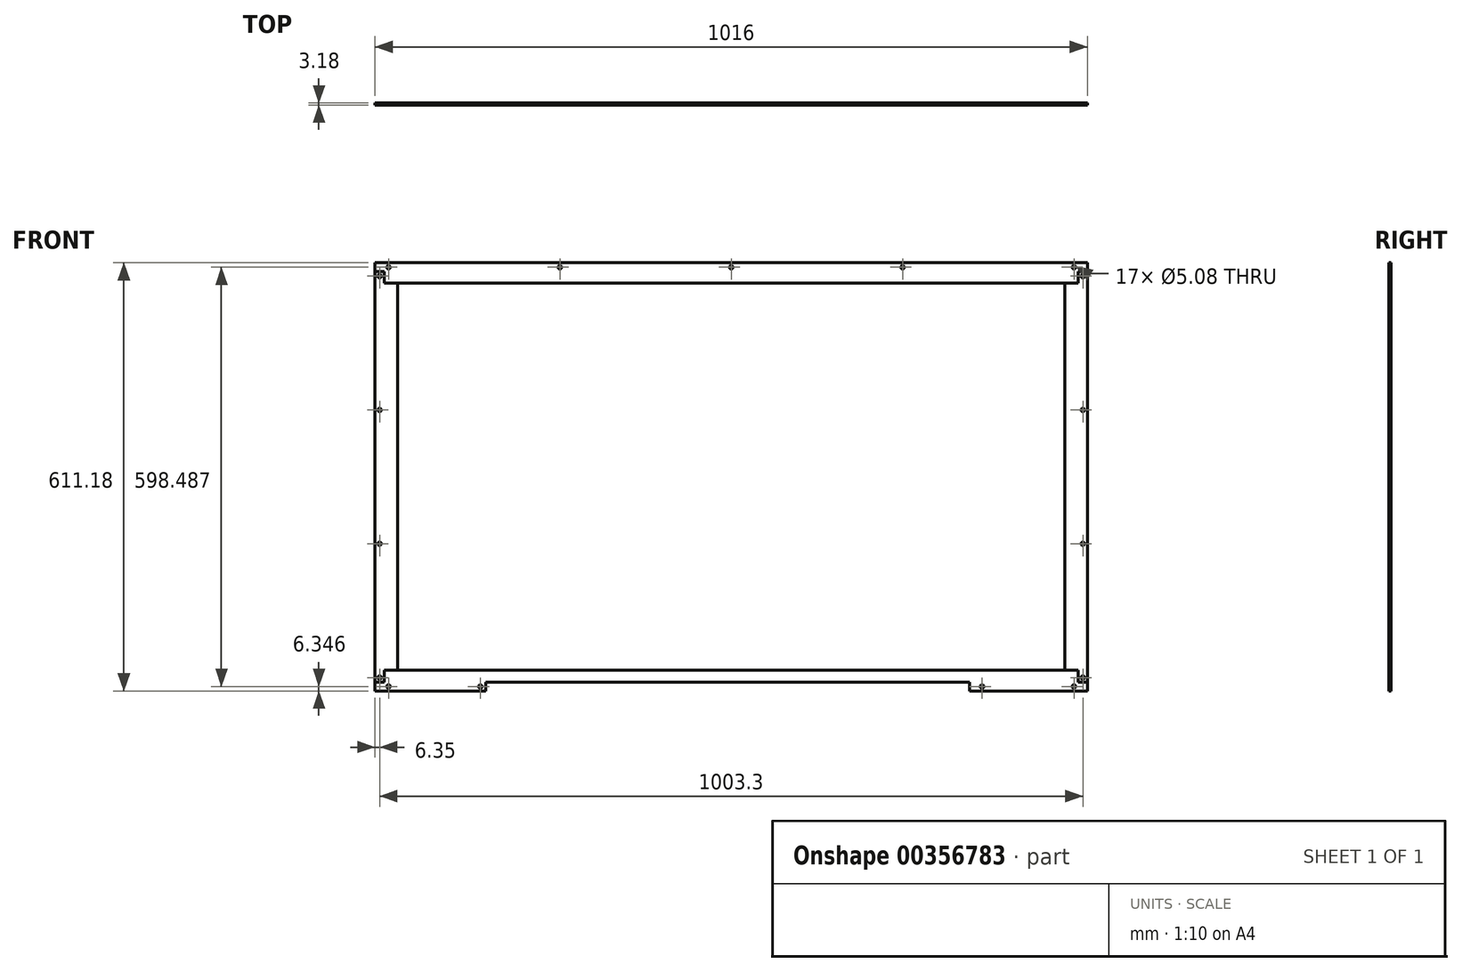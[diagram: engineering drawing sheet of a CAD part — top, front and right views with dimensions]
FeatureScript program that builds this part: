
annotation { "Feature Type Name" : "Feature", "Feature Type Description" : "" }
export const myFeature = defineFeature(function(context is Context, id is Id, definition is map)
    precondition{}
    {
        {
            var Q0;
            Q0=qCreatedBy(makeId("Front.planeOp"),FACE);
            var sketch = newSketch(context, id + "F0", { "sketchPlane" : qUnion([Q0])});
            skLineSegment(sketch, "E0.bottom", {"start": v(495.3, 292.9) * mm, "end": v(-495.3, 292.9) * mm});
            skLineSegment(sketch, "E0.top", {"start": v(495.3, -292.9) * mm, "end": v(-495.3, -292.9) * mm});
            skLineSegment(sketch, "E0.left", {"start": v(495.3, 292.9) * mm, "end": v(495.3, -292.9) * mm});
            skLineSegment(sketch, "E0.right", {"start": v(-495.3, 292.9) * mm, "end": v(-495.3, -292.9) * mm});
            skPoint(sketch, "E0.middle", {"position": v(0, 0) * mm});
            skLineSegment(sketch, "E1.0", {"start": v(-508, 305.6) * mm, "end": v(-508, -305.6) * mm});
            skLineSegment(sketch, "E1.1", {"start": v(508, 305.6) * mm, "end": v(-508, 305.6) * mm});
            skLineSegment(sketch, "E1.2", {"start": v(508, 305.6) * mm, "end": v(508, -305.6) * mm});
            skLineSegment(sketch, "E1.3", {"start": v(508, -305.6) * mm, "end": v(-508, -305.6) * mm});
            skLineSegment(sketch, "E2", {"start": v(-508, 305.6) * mm, "end": v(-495.3, 292.9) * mm});
            skPoint(sketch, "E3.middle", {"position": v(-501.65, 299.24) * mm});
            skLineSegment(sketch, "E4.bottom", {"start": v(-355.3, -296.7) * mm, "end": v(-360.38, -296.7) * mm});
            skLineSegment(sketch, "E4.top", {"start": v(-355.3, -301.78) * mm, "end": v(-360.38, -301.78) * mm});
            skLineSegment(sketch, "E4.left", {"start": v(-355.3, -296.7) * mm, "end": v(-355.3, -301.78) * mm});
            skLineSegment(sketch, "E4.right", {"start": v(-360.38, -296.7) * mm, "end": v(-360.38, -301.78) * mm});
            skPoint(sketch, "E4.middle", {"position": v(-357.84, -299.24) * mm});
            skLineSegment(sketch, "E5.MirrorCS", {"start": v(360.38, -296.7) * mm, "end": v(360.38, -301.78) * mm});
            skLineSegment(sketch, "E6.MirrorCS", {"start": v(355.3, -296.7) * mm, "end": v(360.38, -296.7) * mm});
            skLineSegment(sketch, "E7.MirrorCS", {"start": v(355.3, -296.7) * mm, "end": v(355.3, -301.78) * mm});
            skLineSegment(sketch, "E8.MirrorCS", {"start": v(355.3, -301.78) * mm, "end": v(360.38, -301.78) * mm});
            skLineSegment(sketch, "E9.bottom", {"start": v(-486.41, 296.7) * mm, "end": v(-491.5, 296.7) * mm});
            skLineSegment(sketch, "E9.top", {"start": v(-486.41, 301.78) * mm, "end": v(-491.5, 301.78) * mm});
            skLineSegment(sketch, "E9.left", {"start": v(-486.41, 296.7) * mm, "end": v(-486.41, 301.78) * mm});
            skLineSegment(sketch, "E9.right", {"start": v(-491.5, 296.7) * mm, "end": v(-491.5, 301.78) * mm});
            skPoint(sketch, "E9.middle", {"position": v(-488.95, 299.24) * mm});
            skLineSegment(sketch, "E10.MirrorCS", {"start": v(-504.2, 284) * mm, "end": v(-504.2, 289.08) * mm});
            skLineSegment(sketch, "E11.MirrorCS", {"start": v(-499.11, 289.08) * mm, "end": v(-504.2, 289.08) * mm});
            skLineSegment(sketch, "E12.MirrorCS", {"start": v(-499.11, 284) * mm, "end": v(-499.11, 289.08) * mm});
            skLineSegment(sketch, "E13.MirrorCS", {"start": v(-499.11, 284) * mm, "end": v(-504.2, 284) * mm});
            skCircle(sketch, "E14", {"center": v(-488.95, 299.24) * mm, "radius": 5.97 * mm});
            skLineSegment(sketch, "E15.MirrorCS", {"start": v(499.11, 284) * mm, "end": v(499.11, 289.08) * mm});
            skLineSegment(sketch, "E16.MirrorCS", {"start": v(499.11, 284) * mm, "end": v(504.2, 284) * mm});
            skLineSegment(sketch, "E17.MirrorCS", {"start": v(499.11, 289.08) * mm, "end": v(504.2, 289.08) * mm});
            skLineSegment(sketch, "E18.MirrorCS", {"start": v(504.2, 284) * mm, "end": v(504.2, 289.08) * mm});
            skLineSegment(sketch, "E19.MirrorCS", {"start": v(486.41, 301.78) * mm, "end": v(491.5, 301.78) * mm});
            skLineSegment(sketch, "E20.MirrorCS", {"start": v(486.41, 296.7) * mm, "end": v(486.41, 301.78) * mm});
            skLineSegment(sketch, "E21.MirrorCS", {"start": v(486.41, 296.7) * mm, "end": v(491.5, 296.7) * mm});
            skLineSegment(sketch, "E22.MirrorCS", {"start": v(491.5, 296.7) * mm, "end": v(491.5, 301.78) * mm});
            skPoint(sketch, "E23.MirrorP", {"position": v(488.95, 299.24) * mm});
            skLineSegment(sketch, "E24.MirrorCS", {"start": v(-499.11, -289.08) * mm, "end": v(-504.2, -289.08) * mm});
            skLineSegment(sketch, "E25.MirrorCS", {"start": v(-499.1, -284) * mm, "end": v(-499.1, -289.08) * mm});
            skLineSegment(sketch, "E26.MirrorCS", {"start": v(-499.11, -284) * mm, "end": v(-504.2, -284) * mm});
            skLineSegment(sketch, "E27.MirrorCS", {"start": v(-504.2, -284) * mm, "end": v(-504.2, -289.08) * mm});
            skLineSegment(sketch, "E28.MirrorCS", {"start": v(-486.41, -301.78) * mm, "end": v(-491.5, -301.78) * mm});
            skLineSegment(sketch, "E29.MirrorCS", {"start": v(-491.5, -296.7) * mm, "end": v(-491.5, -301.78) * mm});
            skPoint(sketch, "E30.MirrorP", {"position": v(-488.95, -299.24) * mm});
            skLineSegment(sketch, "E31.MirrorCS", {"start": v(-486.41, -296.7) * mm, "end": v(-486.41, -301.78) * mm});
            skLineSegment(sketch, "E32.MirrorCS", {"start": v(-486.41, -296.7) * mm, "end": v(-491.5, -296.7) * mm});
            skLineSegment(sketch, "E33.MirrorCS", {"start": v(486.41, -296.7) * mm, "end": v(486.41, -301.78) * mm});
            skPoint(sketch, "E34.MirrorP", {"position": v(488.95, -299.24) * mm});
            skLineSegment(sketch, "E35.MirrorCS", {"start": v(491.5, -296.7) * mm, "end": v(491.5, -301.78) * mm});
            skLineSegment(sketch, "E36.MirrorCS", {"start": v(486.41, -296.7) * mm, "end": v(491.5, -296.7) * mm});
            skLineSegment(sketch, "E37.MirrorCS", {"start": v(486.41, -301.78) * mm, "end": v(491.5, -301.78) * mm});
            skLineSegment(sketch, "E38.MirrorCS", {"start": v(499.11, -289.08) * mm, "end": v(504.2, -289.08) * mm});
            skLineSegment(sketch, "E39.MirrorCS", {"start": v(504.2, -284) * mm, "end": v(504.2, -289.08) * mm});
            skLineSegment(sketch, "E40.MirrorCS", {"start": v(499.11, -284) * mm, "end": v(499.11, -289.08) * mm});
            skLineSegment(sketch, "E41.MirrorCS", {"start": v(499.11, -284) * mm, "end": v(504.2, -284) * mm});
            skLineSegment(sketch, "E42.bottom", {"start": v(-504.19, 92.97) * mm, "end": v(-499.11, 92.97) * mm});
            skLineSegment(sketch, "E42.top", {"start": v(-504.19, 98.05) * mm, "end": v(-499.11, 98.05) * mm});
            skLineSegment(sketch, "E42.left", {"start": v(-504.2, 92.97) * mm, "end": v(-504.2, 98.05) * mm});
            skLineSegment(sketch, "E42.right", {"start": v(-499.11, 92.97) * mm, "end": v(-499.11, 98.05) * mm});
            skPoint(sketch, "E42.middle", {"position": v(-501.65, 95.51) * mm});
            skLineSegment(sketch, "E43.bottom", {"start": v(-499.11, -92.97) * mm, "end": v(-504.19, -92.97) * mm});
            skLineSegment(sketch, "E43.top", {"start": v(-499.11, -98.05) * mm, "end": v(-504.19, -98.05) * mm});
            skLineSegment(sketch, "E43.left", {"start": v(-499.11, -92.97) * mm, "end": v(-499.11, -98.05) * mm});
            skLineSegment(sketch, "E43.right", {"start": v(-504.2, -92.97) * mm, "end": v(-504.2, -98.05) * mm});
            skPoint(sketch, "E43.middle", {"position": v(-501.65, -95.51) * mm});
            skLineSegment(sketch, "E44", {"start": v(-501.65, -284) * mm, "end": v(-501.65, -98.05) * mm});
            skLineSegment(sketch, "E45", {"start": v(-501.65, -92.97) * mm, "end": v(-501.65, 92.97) * mm});
            skLineSegment(sketch, "E46", {"start": v(-501.65, 98.05) * mm, "end": v(-501.65, 284) * mm});
            skLineSegment(sketch, "E47.bottom", {"start": v(2.54, 301.78) * mm, "end": v(-2.54, 301.78) * mm});
            skLineSegment(sketch, "E47.top", {"start": v(2.54, 296.7) * mm, "end": v(-2.54, 296.7) * mm});
            skLineSegment(sketch, "E47.left", {"start": v(2.54, 301.78) * mm, "end": v(2.54, 296.7) * mm});
            skLineSegment(sketch, "E47.right", {"start": v(-2.54, 301.78) * mm, "end": v(-2.54, 296.7) * mm});
            skPoint(sketch, "E47.middle", {"position": v(0, 299.24) * mm});
            skPoint(sketch, "E47.middle.positionSnap0", {"position": v(0, 305.6) * mm});
            skPoint(sketch, "E47.centerSnap0", {"position": v(0, 305.6) * mm});
            skLineSegment(sketch, "E48.bottom", {"start": v(-241.94, 301.78) * mm, "end": v(-247.02, 301.78) * mm});
            skLineSegment(sketch, "E48.top", {"start": v(-241.94, 296.7) * mm, "end": v(-247.02, 296.7) * mm});
            skLineSegment(sketch, "E48.left", {"start": v(-241.94, 301.78) * mm, "end": v(-241.94, 296.7) * mm});
            skLineSegment(sketch, "E48.right", {"start": v(-247.02, 301.78) * mm, "end": v(-247.02, 296.7) * mm});
            skPoint(sketch, "E48.middle", {"position": v(-244.48, 299.24) * mm});
            skLineSegment(sketch, "E49.MirrorCS", {"start": v(241.94, 296.7) * mm, "end": v(247.02, 296.7) * mm});
            skPoint(sketch, "E50.MirrorP", {"position": v(244.48, 299.24) * mm});
            skLineSegment(sketch, "E51.MirrorCS", {"start": v(247.02, 301.78) * mm, "end": v(247.02, 296.7) * mm});
            skLineSegment(sketch, "E52.MirrorCS", {"start": v(241.94, 301.78) * mm, "end": v(247.02, 301.78) * mm});
            skLineSegment(sketch, "E53.MirrorCS", {"start": v(241.94, 301.78) * mm, "end": v(241.94, 296.7) * mm});
            skLineSegment(sketch, "E54.MirrorCS", {"start": v(504.19, 92.97) * mm, "end": v(499.11, 92.97) * mm});
            skLineSegment(sketch, "E55.MirrorCS", {"start": v(499.11, 92.97) * mm, "end": v(499.11, 98.05) * mm});
            skPoint(sketch, "E56.MirrorP", {"position": v(501.65, 95.51) * mm});
            skLineSegment(sketch, "E57.MirrorCS", {"start": v(504.19, 98.05) * mm, "end": v(499.11, 98.05) * mm});
            skLineSegment(sketch, "E58.MirrorCS", {"start": v(504.2, 92.97) * mm, "end": v(504.2, 98.05) * mm});
            skLineSegment(sketch, "E59.MirrorCS", {"start": v(499.11, -98.05) * mm, "end": v(504.19, -98.05) * mm});
            skLineSegment(sketch, "E60.MirrorCS", {"start": v(499.11, -92.97) * mm, "end": v(499.11, -98.05) * mm});
            skLineSegment(sketch, "E61.MirrorCS", {"start": v(499.11, -92.97) * mm, "end": v(504.19, -92.97) * mm});
            skPoint(sketch, "E62.MirrorP", {"position": v(501.65, -95.51) * mm});
            skLineSegment(sketch, "E63.MirrorCS", {"start": v(504.2, -92.97) * mm, "end": v(504.2, -98.05) * mm});
            skCircle(sketch, "E64", {"center": v(-488.95, 299.24) * mm, "radius": 2.54 * mm});
            skCircle(sketch, "E65", {"center": v(-501.65, 286.54) * mm, "radius": 2.54 * mm});
            skPoint(sketch, "E65.centerSnap0", {"position": v(-499.11, 286.54) * mm});
            skPoint(sketch, "E65.centerSnap1", {"position": v(-501.65, 289.08) * mm});
            skCircle(sketch, "E66", {"center": v(-501.65, 95.51) * mm, "radius": 2.54 * mm});
            skCircle(sketch, "E67", {"center": v(-501.65, -95.51) * mm, "radius": 2.54 * mm});
            skCircle(sketch, "E68", {"center": v(-501.65, -286.54) * mm, "radius": 2.54 * mm});
            skPoint(sketch, "E68.centerSnap0", {"position": v(-499.11, -286.54) * mm});
            skPoint(sketch, "E68.centerSnap1", {"position": v(-501.65, -289.08) * mm});
            skCircle(sketch, "E69", {"center": v(-488.95, -299.24) * mm, "radius": 2.54 * mm});
            skCircle(sketch, "E70", {"center": v(-357.84, -299.24) * mm, "radius": 2.54 * mm});
            skCircle(sketch, "E71", {"center": v(357.84, -299.24) * mm, "radius": 2.54 * mm});
            skPoint(sketch, "E71.centerSnap0", {"position": v(357.84, -296.7) * mm});
            skCircle(sketch, "E72", {"center": v(488.95, -299.24) * mm, "radius": 2.54 * mm});
            skCircle(sketch, "E73", {"center": v(501.65, -286.54) * mm, "radius": 2.54 * mm});
            skPoint(sketch, "E73.centerSnap0", {"position": v(501.65, -289.08) * mm});
            skPoint(sketch, "E73.centerSnap1", {"position": v(499.11, -286.54) * mm});
            skCircle(sketch, "E74", {"center": v(501.65, -95.51) * mm, "radius": 2.54 * mm});
            skCircle(sketch, "E75", {"center": v(501.65, 95.51) * mm, "radius": 2.54 * mm});
            skCircle(sketch, "E76", {"center": v(501.65, 286.54) * mm, "radius": 2.54 * mm});
            skPoint(sketch, "E76.centerSnap0", {"position": v(504.19, 286.54) * mm});
            skPoint(sketch, "E76.centerSnap1", {"position": v(501.65, 289.08) * mm});
            skCircle(sketch, "E77", {"center": v(488.95, 299.24) * mm, "radius": 2.54 * mm});
            skCircle(sketch, "E78", {"center": v(244.48, 299.24) * mm, "radius": 2.54 * mm});
            skCircle(sketch, "E79", {"center": v(0, 299.24) * mm, "radius": 2.54 * mm});
            skCircle(sketch, "E80", {"center": v(-244.48, 299.24) * mm, "radius": 2.54 * mm});
            skLineSegment(sketch, "E81", {"start": v(-495.3, 292.9) * mm, "end": v(-508, 292.9) * mm});
            skLineSegment(sketch, "E82", {"start": v(495.3, 292.9) * mm, "end": v(508, 292.9) * mm});
            skLineSegment(sketch, "E83", {"start": v(-495.3, -292.9) * mm, "end": v(-508, -292.9) * mm});
            skLineSegment(sketch, "E84", {"start": v(495.3, -292.9) * mm, "end": v(508, -292.9) * mm});
            skLineSegment(sketch, "E85", {"start": v(-350.3, -292.9) * mm, "end": v(-350.3, -305.6) * mm});
            skLineSegment(sketch, "E86", {"start": v(340.3, -292.9) * mm, "end": v(340.3, -305.6) * mm});
            skLineSegment(sketch, "E87.bottom", {"start": v(476, 276.23) * mm, "end": v(-476, 276.23) * mm});
            skLineSegment(sketch, "E87.top", {"start": v(476, -276.22) * mm, "end": v(-476, -276.23) * mm});
            skLineSegment(sketch, "E87.left", {"start": v(476, 276.23) * mm, "end": v(476, -276.23) * mm});
            skLineSegment(sketch, "E87.right", {"start": v(-476, 276.23) * mm, "end": v(-476, -276.23) * mm});
            skLineSegment(sketch, "E88", {"start": v(-350.3, -292.9) * mm, "end": v(-350.3, -276.23) * mm});
            skLineSegment(sketch, "E89", {"start": v(-476, 276.23) * mm, "end": v(-495.3, 276.23) * mm});
            skLineSegment(sketch, "E90", {"start": v(476, 276.23) * mm, "end": v(495.3, 276.23) * mm});
            skLineSegment(sketch, "E91", {"start": v(476, -276.22) * mm, "end": v(495.3, -276.22) * mm});
            skLineSegment(sketch, "E92", {"start": v(-476, -276.23) * mm, "end": v(-495.3, -276.23) * mm});
            skSolve(sketch);
        }
        {
            var Q0;
            {var subQ25=sQuery(id+"F0.wireOp",EDGE,"E81");Q0=makeQuery(id+"F0.imprint","IMPRINT",FACE,{"disambiguationData":[TD([[makeQuery(id+"F0.imprint","IMPRINT",EDGE,{"derivedFrom":subQ25}),1.0]])]});}
            var Q1;
            {var subQ0=sQuery(id+"F0.wireOp",EDGE,"E26.MirrorCS");var subQ1=sQuery(id+"F0.wireOp",EDGE,"E25.MirrorCS");var subQ2=makeQuery(id+"F0.imprint","INTERSECT",VERTEX,{"derivedFrom":[subQ1,subQ0]});Q1=makeQuery(id+"F0.imprint","IMPRINT",FACE,{"disambiguationData":[TD([[makeQuery(id+"F0.imprint","IMPRINT",EDGE,{"disambiguationData":[TD([[subQ2,-1.0]])],"derivedFrom":subQ1}),-1.0]])]});}
            var Q2;
            {var subQ0=sQuery(id+"F0.wireOp",EDGE,"E27.MirrorCS");var subQ1=sQuery(id+"F0.wireOp",EDGE,"E26.MirrorCS");var subQ2=makeQuery(id+"F0.imprint","INTERSECT",VERTEX,{"derivedFrom":[subQ1,subQ0]});Q2=makeQuery(id+"F0.imprint","IMPRINT",FACE,{"disambiguationData":[TD([[makeQuery(id+"F0.imprint","IMPRINT",EDGE,{"disambiguationData":[TD([[subQ2,1.0]])],"derivedFrom":subQ1}),1.0]])]});}
            var Q3;
            {var subQ0=sQuery(id+"F0.wireOp",EDGE,"E27.MirrorCS");var subQ1=sQuery(id+"F0.wireOp",EDGE,"E24.MirrorCS");var subQ2=makeQuery(id+"F0.imprint","INTERSECT",VERTEX,{"derivedFrom":[subQ1,subQ0]});Q3=makeQuery(id+"F0.imprint","IMPRINT",FACE,{"disambiguationData":[TD([[makeQuery(id+"F0.imprint","IMPRINT",EDGE,{"disambiguationData":[TD([[subQ2,1.0]])],"derivedFrom":subQ1}),-1.0]])]});}
            var Q4;
            {var subQ0=sQuery(id+"F0.wireOp",EDGE,"E25.MirrorCS");var subQ1=sQuery(id+"F0.wireOp",EDGE,"E24.MirrorCS");var subQ2=makeQuery(id+"F0.imprint","INTERSECT",VERTEX,{"derivedFrom":[subQ1,subQ0]});Q4=makeQuery(id+"F0.imprint","IMPRINT",FACE,{"disambiguationData":[TD([[makeQuery(id+"F0.imprint","IMPRINT",EDGE,{"disambiguationData":[TD([[subQ2,-1.0]])],"derivedFrom":subQ1}),-1.0]])]});}
            var Q5;
            Q5=makeQuery(id+"F0.imprint","IMPRINT",FACE,{"disambiguationData":[TD([[makeQuery(id+"F0.imprint","IMPRINT",EDGE,{"derivedFrom":sQuery(id+"F0.wireOp",EDGE,"E87.right")}),-1.0]])]});
            var Q6;
            {var subQ0=sQuery(id+"F0.wireOp",EDGE,"E43.right");var subQ1=sQuery(id+"F0.wireOp",EDGE,"E43.top");var subQ2=makeQuery(id+"F0.imprint","INTERSECT",VERTEX,{"derivedFrom":[subQ1,subQ0]});Q6=makeQuery(id+"F0.imprint","IMPRINT",FACE,{"disambiguationData":[TD([[makeQuery(id+"F0.imprint","IMPRINT",EDGE,{"disambiguationData":[TD([[subQ2,1.0]])],"derivedFrom":subQ1}),-1.0]])]});}
            var Q7;
            {var subQ0=sQuery(id+"F0.wireOp",EDGE,"E43.left");var subQ1=sQuery(id+"F0.wireOp",EDGE,"E43.top");var subQ2=makeQuery(id+"F0.imprint","INTERSECT",VERTEX,{"derivedFrom":[subQ1,subQ0]});Q7=makeQuery(id+"F0.imprint","IMPRINT",FACE,{"disambiguationData":[TD([[makeQuery(id+"F0.imprint","IMPRINT",EDGE,{"disambiguationData":[TD([[subQ2,-1.0]])],"derivedFrom":subQ1}),-1.0]])]});}
            var Q8;
            {var subQ0=sQuery(id+"F0.wireOp",EDGE,"E43.left");var subQ1=sQuery(id+"F0.wireOp",EDGE,"E43.bottom");var subQ2=makeQuery(id+"F0.imprint","INTERSECT",VERTEX,{"derivedFrom":[subQ1,subQ0]});Q8=makeQuery(id+"F0.imprint","IMPRINT",FACE,{"disambiguationData":[TD([[makeQuery(id+"F0.imprint","IMPRINT",EDGE,{"disambiguationData":[TD([[subQ2,-1.0]])],"derivedFrom":subQ1}),1.0]])]});}
            var Q9;
            {var subQ0=sQuery(id+"F0.wireOp",EDGE,"E43.right");var subQ1=sQuery(id+"F0.wireOp",EDGE,"E43.bottom");var subQ2=makeQuery(id+"F0.imprint","INTERSECT",VERTEX,{"derivedFrom":[subQ1,subQ0]});Q9=makeQuery(id+"F0.imprint","IMPRINT",FACE,{"disambiguationData":[TD([[makeQuery(id+"F0.imprint","IMPRINT",EDGE,{"disambiguationData":[TD([[subQ2,1.0]])],"derivedFrom":subQ1}),1.0]])]});}
            var Q10;
            {var subQ0=sQuery(id+"F0.wireOp",EDGE,"E42.left");var subQ1=sQuery(id+"F0.wireOp",EDGE,"E42.top");var subQ2=makeQuery(id+"F0.imprint","INTERSECT",VERTEX,{"derivedFrom":[subQ1,subQ0]});Q10=makeQuery(id+"F0.imprint","IMPRINT",FACE,{"disambiguationData":[TD([[makeQuery(id+"F0.imprint","IMPRINT",EDGE,{"disambiguationData":[TD([[subQ2,-1.0]])],"derivedFrom":subQ1}),-1.0]])]});}
            var Q11;
            {var subQ0=sQuery(id+"F0.wireOp",EDGE,"E42.right");var subQ1=sQuery(id+"F0.wireOp",EDGE,"E42.top");var subQ2=makeQuery(id+"F0.imprint","INTERSECT",VERTEX,{"derivedFrom":[subQ1,subQ0]});Q11=makeQuery(id+"F0.imprint","IMPRINT",FACE,{"disambiguationData":[TD([[makeQuery(id+"F0.imprint","IMPRINT",EDGE,{"disambiguationData":[TD([[subQ2,1.0]])],"derivedFrom":subQ1}),-1.0]])]});}
            var Q12;
            {var subQ0=sQuery(id+"F0.wireOp",EDGE,"E42.right");var subQ1=sQuery(id+"F0.wireOp",EDGE,"E42.bottom");var subQ2=makeQuery(id+"F0.imprint","INTERSECT",VERTEX,{"derivedFrom":[subQ1,subQ0]});Q12=makeQuery(id+"F0.imprint","IMPRINT",FACE,{"disambiguationData":[TD([[makeQuery(id+"F0.imprint","IMPRINT",EDGE,{"disambiguationData":[TD([[subQ2,1.0]])],"derivedFrom":subQ1}),1.0]])]});}
            var Q13;
            {var subQ0=sQuery(id+"F0.wireOp",EDGE,"E42.left");var subQ1=sQuery(id+"F0.wireOp",EDGE,"E42.bottom");var subQ2=makeQuery(id+"F0.imprint","INTERSECT",VERTEX,{"derivedFrom":[subQ1,subQ0]});Q13=makeQuery(id+"F0.imprint","IMPRINT",FACE,{"disambiguationData":[TD([[makeQuery(id+"F0.imprint","IMPRINT",EDGE,{"disambiguationData":[TD([[subQ2,-1.0]])],"derivedFrom":subQ1}),1.0]])]});}
            var Q14;
            {var subQ0=sQuery(id+"F0.wireOp",EDGE,"E11.MirrorCS");var subQ1=sQuery(id+"F0.wireOp",EDGE,"E10.MirrorCS");var subQ2=makeQuery(id+"F0.imprint","INTERSECT",VERTEX,{"derivedFrom":[subQ1,subQ0]});Q14=makeQuery(id+"F0.imprint","IMPRINT",FACE,{"disambiguationData":[TD([[makeQuery(id+"F0.imprint","IMPRINT",EDGE,{"disambiguationData":[TD([[subQ2,1.0]])],"derivedFrom":subQ1}),-1.0]])]});}
            var Q15;
            {var subQ0=sQuery(id+"F0.wireOp",EDGE,"E12.MirrorCS");var subQ1=sQuery(id+"F0.wireOp",EDGE,"E11.MirrorCS");var subQ2=makeQuery(id+"F0.imprint","INTERSECT",VERTEX,{"derivedFrom":[subQ1,subQ0]});Q15=makeQuery(id+"F0.imprint","IMPRINT",FACE,{"disambiguationData":[TD([[makeQuery(id+"F0.imprint","IMPRINT",EDGE,{"disambiguationData":[TD([[subQ2,-1.0]])],"derivedFrom":subQ1}),1.0]])]});}
            var Q16;
            {var subQ0=sQuery(id+"F0.wireOp",EDGE,"E13.MirrorCS");var subQ1=sQuery(id+"F0.wireOp",EDGE,"E12.MirrorCS");var subQ2=makeQuery(id+"F0.imprint","INTERSECT",VERTEX,{"derivedFrom":[subQ1,subQ0]});Q16=makeQuery(id+"F0.imprint","IMPRINT",FACE,{"disambiguationData":[TD([[makeQuery(id+"F0.imprint","IMPRINT",EDGE,{"disambiguationData":[TD([[subQ2,-1.0]])],"derivedFrom":subQ1}),1.0]])]});}
            var Q17;
            {var subQ0=sQuery(id+"F0.wireOp",EDGE,"E13.MirrorCS");var subQ1=sQuery(id+"F0.wireOp",EDGE,"E10.MirrorCS");var subQ2=makeQuery(id+"F0.imprint","INTERSECT",VERTEX,{"derivedFrom":[subQ1,subQ0]});Q17=makeQuery(id+"F0.imprint","IMPRINT",FACE,{"disambiguationData":[TD([[makeQuery(id+"F0.imprint","IMPRINT",EDGE,{"disambiguationData":[TD([[subQ2,-1.0]])],"derivedFrom":subQ1}),-1.0]])]});}
            extrude(context, id + "F1", {"entities" : qUnion([Q0, Q1, Q2, Q3, Q4, Q5, Q6, Q7, Q8, Q9, Q10, Q11, Q12, Q13, Q14, Q15, Q16, Q17]), "endBound" : BoundingType.SYMMETRIC, "depth" : 3.17 * mm});
        }
        {
            var Q0;
            {var subQ1=sQuery(id+"F0.wireOp",EDGE,"E0.bottom");Q0=makeQuery(id+"F0.imprint","IMPRINT",FACE,{"disambiguationData":[TD([[makeQuery(id+"F0.imprint","IMPRINT",EDGE,{"derivedFrom":subQ1}),1.0]])]});}
            var Q1;
            {var subQ0=sQuery(id+"F0.wireOp",EDGE,"E2");Q1=makeQuery(id+"F0.imprint","IMPRINT",FACE,{"disambiguationData":[TD([[makeQuery(id+"F0.imprint","IMPRINT",EDGE,{"derivedFrom":subQ0}),-1.0]])]});}
            var Q2;
            Q2=makeQuery(id+"F0.imprint","IMPRINT",FACE,{"disambiguationData":[TD([[makeQuery(id+"F0.imprint","IMPRINT",EDGE,{"derivedFrom":sQuery(id+"F0.wireOp",EDGE,"E0.bottom")}),-1.0]])]});
            var Q3;
            Q3=makeQuery(id+"F0.imprint","IMPRINT",FACE,{"disambiguationData":[TD([[makeQuery(id+"F0.imprint","IMPRINT",EDGE,{"derivedFrom":sQuery(id+"F0.wireOp",EDGE,"E14")}),1.0]])]});
            var Q4;
            {var subQ0=sQuery(id+"F0.wireOp",EDGE,"E9.right");var subQ1=sQuery(id+"F0.wireOp",EDGE,"E9.top");var subQ2=makeQuery(id+"F0.imprint","INTERSECT",VERTEX,{"derivedFrom":[subQ1,subQ0]});Q4=makeQuery(id+"F0.imprint","IMPRINT",FACE,{"disambiguationData":[TD([[makeQuery(id+"F0.imprint","IMPRINT",EDGE,{"disambiguationData":[TD([[subQ2,1.0]])],"derivedFrom":subQ1}),1.0]])]});}
            var Q5;
            {var subQ0=sQuery(id+"F0.wireOp",EDGE,"E9.left");var subQ1=sQuery(id+"F0.wireOp",EDGE,"E9.top");var subQ2=makeQuery(id+"F0.imprint","INTERSECT",VERTEX,{"derivedFrom":[subQ1,subQ0]});Q5=makeQuery(id+"F0.imprint","IMPRINT",FACE,{"disambiguationData":[TD([[makeQuery(id+"F0.imprint","IMPRINT",EDGE,{"disambiguationData":[TD([[subQ2,-1.0]])],"derivedFrom":subQ1}),1.0]])]});}
            var Q6;
            {var subQ0=sQuery(id+"F0.wireOp",EDGE,"E9.left");var subQ1=sQuery(id+"F0.wireOp",EDGE,"E9.bottom");var subQ2=makeQuery(id+"F0.imprint","INTERSECT",VERTEX,{"derivedFrom":[subQ1,subQ0]});Q6=makeQuery(id+"F0.imprint","IMPRINT",FACE,{"disambiguationData":[TD([[makeQuery(id+"F0.imprint","IMPRINT",EDGE,{"disambiguationData":[TD([[subQ2,-1.0]])],"derivedFrom":subQ1}),-1.0]])]});}
            var Q7;
            {var subQ0=sQuery(id+"F0.wireOp",EDGE,"E9.right");var subQ1=sQuery(id+"F0.wireOp",EDGE,"E9.bottom");var subQ2=makeQuery(id+"F0.imprint","INTERSECT",VERTEX,{"derivedFrom":[subQ1,subQ0]});Q7=makeQuery(id+"F0.imprint","IMPRINT",FACE,{"disambiguationData":[TD([[makeQuery(id+"F0.imprint","IMPRINT",EDGE,{"disambiguationData":[TD([[subQ2,1.0]])],"derivedFrom":subQ1}),-1.0]])]});}
            var Q8;
            {var subQ0=sQuery(id+"F0.wireOp",EDGE,"E48.right");var subQ1=sQuery(id+"F0.wireOp",EDGE,"E48.bottom");var subQ2=makeQuery(id+"F0.imprint","INTERSECT",VERTEX,{"derivedFrom":[subQ1,subQ0]});Q8=makeQuery(id+"F0.imprint","IMPRINT",FACE,{"disambiguationData":[TD([[makeQuery(id+"F0.imprint","IMPRINT",EDGE,{"disambiguationData":[TD([[subQ2,1.0]])],"derivedFrom":subQ1}),1.0]])]});}
            var Q9;
            {var subQ0=sQuery(id+"F0.wireOp",EDGE,"E48.right");var subQ1=sQuery(id+"F0.wireOp",EDGE,"E48.top");var subQ2=makeQuery(id+"F0.imprint","INTERSECT",VERTEX,{"derivedFrom":[subQ1,subQ0]});Q9=makeQuery(id+"F0.imprint","IMPRINT",FACE,{"disambiguationData":[TD([[makeQuery(id+"F0.imprint","IMPRINT",EDGE,{"disambiguationData":[TD([[subQ2,1.0]])],"derivedFrom":subQ1}),-1.0]])]});}
            var Q10;
            {var subQ0=sQuery(id+"F0.wireOp",EDGE,"E48.left");var subQ1=sQuery(id+"F0.wireOp",EDGE,"E48.top");var subQ2=makeQuery(id+"F0.imprint","INTERSECT",VERTEX,{"derivedFrom":[subQ1,subQ0]});Q10=makeQuery(id+"F0.imprint","IMPRINT",FACE,{"disambiguationData":[TD([[makeQuery(id+"F0.imprint","IMPRINT",EDGE,{"disambiguationData":[TD([[subQ2,-1.0]])],"derivedFrom":subQ1}),-1.0]])]});}
            var Q11;
            {var subQ0=sQuery(id+"F0.wireOp",EDGE,"E48.left");var subQ1=sQuery(id+"F0.wireOp",EDGE,"E48.bottom");var subQ2=makeQuery(id+"F0.imprint","INTERSECT",VERTEX,{"derivedFrom":[subQ1,subQ0]});Q11=makeQuery(id+"F0.imprint","IMPRINT",FACE,{"disambiguationData":[TD([[makeQuery(id+"F0.imprint","IMPRINT",EDGE,{"disambiguationData":[TD([[subQ2,-1.0]])],"derivedFrom":subQ1}),1.0]])]});}
            var Q12;
            {var subQ0=sQuery(id+"F0.wireOp",EDGE,"E47.right");var subQ1=sQuery(id+"F0.wireOp",EDGE,"E47.bottom");var subQ2=makeQuery(id+"F0.imprint","INTERSECT",VERTEX,{"derivedFrom":[subQ1,subQ0]});Q12=makeQuery(id+"F0.imprint","IMPRINT",FACE,{"disambiguationData":[TD([[makeQuery(id+"F0.imprint","IMPRINT",EDGE,{"disambiguationData":[TD([[subQ2,1.0]])],"derivedFrom":subQ1}),1.0]])]});}
            var Q13;
            {var subQ0=sQuery(id+"F0.wireOp",EDGE,"E47.left");var subQ1=sQuery(id+"F0.wireOp",EDGE,"E47.bottom");var subQ2=makeQuery(id+"F0.imprint","INTERSECT",VERTEX,{"derivedFrom":[subQ1,subQ0]});Q13=makeQuery(id+"F0.imprint","IMPRINT",FACE,{"disambiguationData":[TD([[makeQuery(id+"F0.imprint","IMPRINT",EDGE,{"disambiguationData":[TD([[subQ2,-1.0]])],"derivedFrom":subQ1}),1.0]])]});}
            var Q14;
            {var subQ0=sQuery(id+"F0.wireOp",EDGE,"E47.left");var subQ1=sQuery(id+"F0.wireOp",EDGE,"E47.top");var subQ2=makeQuery(id+"F0.imprint","INTERSECT",VERTEX,{"derivedFrom":[subQ1,subQ0]});Q14=makeQuery(id+"F0.imprint","IMPRINT",FACE,{"disambiguationData":[TD([[makeQuery(id+"F0.imprint","IMPRINT",EDGE,{"disambiguationData":[TD([[subQ2,-1.0]])],"derivedFrom":subQ1}),-1.0]])]});}
            var Q15;
            {var subQ0=sQuery(id+"F0.wireOp",EDGE,"E47.right");var subQ1=sQuery(id+"F0.wireOp",EDGE,"E47.top");var subQ2=makeQuery(id+"F0.imprint","INTERSECT",VERTEX,{"derivedFrom":[subQ1,subQ0]});Q15=makeQuery(id+"F0.imprint","IMPRINT",FACE,{"disambiguationData":[TD([[makeQuery(id+"F0.imprint","IMPRINT",EDGE,{"disambiguationData":[TD([[subQ2,1.0]])],"derivedFrom":subQ1}),-1.0]])]});}
            var Q16;
            {var subQ0=sQuery(id+"F0.wireOp",EDGE,"E53.MirrorCS");var subQ1=sQuery(id+"F0.wireOp",EDGE,"E52.MirrorCS");var subQ2=makeQuery(id+"F0.imprint","INTERSECT",VERTEX,{"derivedFrom":[subQ1,subQ0]});Q16=makeQuery(id+"F0.imprint","IMPRINT",FACE,{"disambiguationData":[TD([[makeQuery(id+"F0.imprint","IMPRINT",EDGE,{"disambiguationData":[TD([[subQ2,-1.0]])],"derivedFrom":subQ1}),-1.0]])]});}
            var Q17;
            {var subQ0=sQuery(id+"F0.wireOp",EDGE,"E52.MirrorCS");var subQ1=sQuery(id+"F0.wireOp",EDGE,"E51.MirrorCS");var subQ2=makeQuery(id+"F0.imprint","INTERSECT",VERTEX,{"derivedFrom":[subQ1,subQ0]});Q17=makeQuery(id+"F0.imprint","IMPRINT",FACE,{"disambiguationData":[TD([[makeQuery(id+"F0.imprint","IMPRINT",EDGE,{"disambiguationData":[TD([[subQ2,-1.0]])],"derivedFrom":subQ1}),-1.0]])]});}
            var Q18;
            {var subQ0=sQuery(id+"F0.wireOp",EDGE,"E51.MirrorCS");var subQ1=sQuery(id+"F0.wireOp",EDGE,"E49.MirrorCS");var subQ2=makeQuery(id+"F0.imprint","INTERSECT",VERTEX,{"derivedFrom":[subQ1,subQ0]});Q18=makeQuery(id+"F0.imprint","IMPRINT",FACE,{"disambiguationData":[TD([[makeQuery(id+"F0.imprint","IMPRINT",EDGE,{"disambiguationData":[TD([[subQ2,1.0]])],"derivedFrom":subQ1}),1.0]])]});}
            var Q19;
            {var subQ0=sQuery(id+"F0.wireOp",EDGE,"E53.MirrorCS");var subQ1=sQuery(id+"F0.wireOp",EDGE,"E49.MirrorCS");var subQ2=makeQuery(id+"F0.imprint","INTERSECT",VERTEX,{"derivedFrom":[subQ1,subQ0]});Q19=makeQuery(id+"F0.imprint","IMPRINT",FACE,{"disambiguationData":[TD([[makeQuery(id+"F0.imprint","IMPRINT",EDGE,{"disambiguationData":[TD([[subQ2,-1.0]])],"derivedFrom":subQ1}),1.0]])]});}
            var Q20;
            {var subQ0=sQuery(id+"F0.wireOp",EDGE,"E20.MirrorCS");var subQ1=sQuery(id+"F0.wireOp",EDGE,"E19.MirrorCS");var subQ2=makeQuery(id+"F0.imprint","INTERSECT",VERTEX,{"derivedFrom":[subQ1,subQ0]});Q20=makeQuery(id+"F0.imprint","IMPRINT",FACE,{"disambiguationData":[TD([[makeQuery(id+"F0.imprint","IMPRINT",EDGE,{"disambiguationData":[TD([[subQ2,-1.0]])],"derivedFrom":subQ1}),-1.0]])]});}
            var Q21;
            {var subQ0=sQuery(id+"F0.wireOp",EDGE,"E22.MirrorCS");var subQ1=sQuery(id+"F0.wireOp",EDGE,"E19.MirrorCS");var subQ2=makeQuery(id+"F0.imprint","INTERSECT",VERTEX,{"derivedFrom":[subQ1,subQ0]});Q21=makeQuery(id+"F0.imprint","IMPRINT",FACE,{"disambiguationData":[TD([[makeQuery(id+"F0.imprint","IMPRINT",EDGE,{"disambiguationData":[TD([[subQ2,1.0]])],"derivedFrom":subQ1}),-1.0]])]});}
            var Q22;
            {var subQ0=sQuery(id+"F0.wireOp",EDGE,"E22.MirrorCS");var subQ1=sQuery(id+"F0.wireOp",EDGE,"E21.MirrorCS");var subQ2=makeQuery(id+"F0.imprint","INTERSECT",VERTEX,{"derivedFrom":[subQ1,subQ0]});Q22=makeQuery(id+"F0.imprint","IMPRINT",FACE,{"disambiguationData":[TD([[makeQuery(id+"F0.imprint","IMPRINT",EDGE,{"disambiguationData":[TD([[subQ2,1.0]])],"derivedFrom":subQ1}),1.0]])]});}
            var Q23;
            {var subQ0=sQuery(id+"F0.wireOp",EDGE,"E21.MirrorCS");var subQ1=sQuery(id+"F0.wireOp",EDGE,"E20.MirrorCS");var subQ2=makeQuery(id+"F0.imprint","INTERSECT",VERTEX,{"derivedFrom":[subQ1,subQ0]});Q23=makeQuery(id+"F0.imprint","IMPRINT",FACE,{"disambiguationData":[TD([[makeQuery(id+"F0.imprint","IMPRINT",EDGE,{"disambiguationData":[TD([[subQ2,-1.0]])],"derivedFrom":subQ1}),-1.0]])]});}
            extrude(context, id + "F2", {"entities" : qUnion([Q0, Q1, Q2, Q3, Q4, Q5, Q6, Q7, Q8, Q9, Q10, Q11, Q12, Q13, Q14, Q15, Q16, Q17, Q18, Q19, Q20, Q21, Q22, Q23]), "endBound" : BoundingType.SYMMETRIC, "depth" : 3.17 * mm});
        }
        {
            var Q0;
            {var subQ31=sQuery(id+"F0.wireOp",EDGE,"E82");Q0=makeQuery(id+"F0.imprint","IMPRINT",FACE,{"disambiguationData":[TD([[makeQuery(id+"F0.imprint","IMPRINT",EDGE,{"derivedFrom":subQ31}),-1.0]])]});}
            var Q1;
            {var subQ0=sQuery(id+"F0.wireOp",EDGE,"E41.MirrorCS");var subQ1=sQuery(id+"F0.wireOp",EDGE,"E39.MirrorCS");var subQ2=makeQuery(id+"F0.imprint","INTERSECT",VERTEX,{"derivedFrom":[subQ1,subQ0]});Q1=makeQuery(id+"F0.imprint","IMPRINT",FACE,{"disambiguationData":[TD([[makeQuery(id+"F0.imprint","IMPRINT",EDGE,{"disambiguationData":[TD([[subQ2,-1.0]])],"derivedFrom":subQ1}),-1.0]])]});}
            var Q2;
            {var subQ0=sQuery(id+"F0.wireOp",EDGE,"E39.MirrorCS");var subQ1=sQuery(id+"F0.wireOp",EDGE,"E38.MirrorCS");var subQ2=makeQuery(id+"F0.imprint","INTERSECT",VERTEX,{"derivedFrom":[subQ1,subQ0]});Q2=makeQuery(id+"F0.imprint","IMPRINT",FACE,{"disambiguationData":[TD([[makeQuery(id+"F0.imprint","IMPRINT",EDGE,{"disambiguationData":[TD([[subQ2,1.0]])],"derivedFrom":subQ1}),1.0]])]});}
            var Q3;
            {var subQ0=sQuery(id+"F0.wireOp",EDGE,"E40.MirrorCS");var subQ1=sQuery(id+"F0.wireOp",EDGE,"E38.MirrorCS");var subQ2=makeQuery(id+"F0.imprint","INTERSECT",VERTEX,{"derivedFrom":[subQ1,subQ0]});Q3=makeQuery(id+"F0.imprint","IMPRINT",FACE,{"disambiguationData":[TD([[makeQuery(id+"F0.imprint","IMPRINT",EDGE,{"disambiguationData":[TD([[subQ2,-1.0]])],"derivedFrom":subQ1}),1.0]])]});}
            var Q4;
            {var subQ0=sQuery(id+"F0.wireOp",EDGE,"E41.MirrorCS");var subQ1=sQuery(id+"F0.wireOp",EDGE,"E40.MirrorCS");var subQ2=makeQuery(id+"F0.imprint","INTERSECT",VERTEX,{"derivedFrom":[subQ1,subQ0]});Q4=makeQuery(id+"F0.imprint","IMPRINT",FACE,{"disambiguationData":[TD([[makeQuery(id+"F0.imprint","IMPRINT",EDGE,{"disambiguationData":[TD([[subQ2,-1.0]])],"derivedFrom":subQ1}),1.0]])]});}
            var Q5;
            Q5=makeQuery(id+"F0.imprint","IMPRINT",FACE,{"disambiguationData":[TD([[makeQuery(id+"F0.imprint","IMPRINT",EDGE,{"derivedFrom":sQuery(id+"F0.wireOp",EDGE,"E87.left")}),1.0]])]});
            var Q6;
            {var subQ0=sQuery(id+"F0.wireOp",EDGE,"E57.MirrorCS");var subQ1=sQuery(id+"F0.wireOp",EDGE,"E55.MirrorCS");var subQ2=makeQuery(id+"F0.imprint","INTERSECT",VERTEX,{"derivedFrom":[subQ1,subQ0]});Q6=makeQuery(id+"F0.imprint","IMPRINT",FACE,{"disambiguationData":[TD([[makeQuery(id+"F0.imprint","IMPRINT",EDGE,{"disambiguationData":[TD([[subQ2,1.0]])],"derivedFrom":subQ1}),-1.0]])]});}
            var Q7;
            {var subQ0=sQuery(id+"F0.wireOp",EDGE,"E58.MirrorCS");var subQ1=sQuery(id+"F0.wireOp",EDGE,"E57.MirrorCS");var subQ2=makeQuery(id+"F0.imprint","INTERSECT",VERTEX,{"derivedFrom":[subQ1,subQ0]});Q7=makeQuery(id+"F0.imprint","IMPRINT",FACE,{"disambiguationData":[TD([[makeQuery(id+"F0.imprint","IMPRINT",EDGE,{"disambiguationData":[TD([[subQ2,-1.0]])],"derivedFrom":subQ1}),1.0]])]});}
            var Q8;
            {var subQ0=sQuery(id+"F0.wireOp",EDGE,"E58.MirrorCS");var subQ1=sQuery(id+"F0.wireOp",EDGE,"E54.MirrorCS");var subQ2=makeQuery(id+"F0.imprint","INTERSECT",VERTEX,{"derivedFrom":[subQ1,subQ0]});Q8=makeQuery(id+"F0.imprint","IMPRINT",FACE,{"disambiguationData":[TD([[makeQuery(id+"F0.imprint","IMPRINT",EDGE,{"disambiguationData":[TD([[subQ2,-1.0]])],"derivedFrom":subQ1}),-1.0]])]});}
            var Q9;
            {var subQ0=sQuery(id+"F0.wireOp",EDGE,"E55.MirrorCS");var subQ1=sQuery(id+"F0.wireOp",EDGE,"E54.MirrorCS");var subQ2=makeQuery(id+"F0.imprint","INTERSECT",VERTEX,{"derivedFrom":[subQ1,subQ0]});Q9=makeQuery(id+"F0.imprint","IMPRINT",FACE,{"disambiguationData":[TD([[makeQuery(id+"F0.imprint","IMPRINT",EDGE,{"disambiguationData":[TD([[subQ2,1.0]])],"derivedFrom":subQ1}),-1.0]])]});}
            var Q10;
            {var subQ0=sQuery(id+"F0.wireOp",EDGE,"E60.MirrorCS");var subQ1=sQuery(id+"F0.wireOp",EDGE,"E59.MirrorCS");var subQ2=makeQuery(id+"F0.imprint","INTERSECT",VERTEX,{"derivedFrom":[subQ1,subQ0]});Q10=makeQuery(id+"F0.imprint","IMPRINT",FACE,{"disambiguationData":[TD([[makeQuery(id+"F0.imprint","IMPRINT",EDGE,{"disambiguationData":[TD([[subQ2,-1.0]])],"derivedFrom":subQ1}),1.0]])]});}
            var Q11;
            {var subQ0=sQuery(id+"F0.wireOp",EDGE,"E61.MirrorCS");var subQ1=sQuery(id+"F0.wireOp",EDGE,"E60.MirrorCS");var subQ2=makeQuery(id+"F0.imprint","INTERSECT",VERTEX,{"derivedFrom":[subQ1,subQ0]});Q11=makeQuery(id+"F0.imprint","IMPRINT",FACE,{"disambiguationData":[TD([[makeQuery(id+"F0.imprint","IMPRINT",EDGE,{"disambiguationData":[TD([[subQ2,-1.0]])],"derivedFrom":subQ1}),1.0]])]});}
            var Q12;
            {var subQ0=sQuery(id+"F0.wireOp",EDGE,"E63.MirrorCS");var subQ1=sQuery(id+"F0.wireOp",EDGE,"E61.MirrorCS");var subQ2=makeQuery(id+"F0.imprint","INTERSECT",VERTEX,{"derivedFrom":[subQ1,subQ0]});Q12=makeQuery(id+"F0.imprint","IMPRINT",FACE,{"disambiguationData":[TD([[makeQuery(id+"F0.imprint","IMPRINT",EDGE,{"disambiguationData":[TD([[subQ2,1.0]])],"derivedFrom":subQ1}),-1.0]])]});}
            var Q13;
            {var subQ0=sQuery(id+"F0.wireOp",EDGE,"E63.MirrorCS");var subQ1=sQuery(id+"F0.wireOp",EDGE,"E59.MirrorCS");var subQ2=makeQuery(id+"F0.imprint","INTERSECT",VERTEX,{"derivedFrom":[subQ1,subQ0]});Q13=makeQuery(id+"F0.imprint","IMPRINT",FACE,{"disambiguationData":[TD([[makeQuery(id+"F0.imprint","IMPRINT",EDGE,{"disambiguationData":[TD([[subQ2,1.0]])],"derivedFrom":subQ1}),1.0]])]});}
            var Q14;
            {var subQ0=sQuery(id+"F0.wireOp",EDGE,"E16.MirrorCS");var subQ1=sQuery(id+"F0.wireOp",EDGE,"E15.MirrorCS");var subQ2=makeQuery(id+"F0.imprint","INTERSECT",VERTEX,{"derivedFrom":[subQ1,subQ0]});Q14=makeQuery(id+"F0.imprint","IMPRINT",FACE,{"disambiguationData":[TD([[makeQuery(id+"F0.imprint","IMPRINT",EDGE,{"disambiguationData":[TD([[subQ2,-1.0]])],"derivedFrom":subQ1}),-1.0]])]});}
            var Q15;
            {var subQ0=sQuery(id+"F0.wireOp",EDGE,"E17.MirrorCS");var subQ1=sQuery(id+"F0.wireOp",EDGE,"E15.MirrorCS");var subQ2=makeQuery(id+"F0.imprint","INTERSECT",VERTEX,{"derivedFrom":[subQ1,subQ0]});Q15=makeQuery(id+"F0.imprint","IMPRINT",FACE,{"disambiguationData":[TD([[makeQuery(id+"F0.imprint","IMPRINT",EDGE,{"disambiguationData":[TD([[subQ2,1.0]])],"derivedFrom":subQ1}),-1.0]])]});}
            var Q16;
            {var subQ0=sQuery(id+"F0.wireOp",EDGE,"E18.MirrorCS");var subQ1=sQuery(id+"F0.wireOp",EDGE,"E17.MirrorCS");var subQ2=makeQuery(id+"F0.imprint","INTERSECT",VERTEX,{"derivedFrom":[subQ1,subQ0]});Q16=makeQuery(id+"F0.imprint","IMPRINT",FACE,{"disambiguationData":[TD([[makeQuery(id+"F0.imprint","IMPRINT",EDGE,{"disambiguationData":[TD([[subQ2,1.0]])],"derivedFrom":subQ1}),-1.0]])]});}
            var Q17;
            {var subQ0=sQuery(id+"F0.wireOp",EDGE,"E18.MirrorCS");var subQ1=sQuery(id+"F0.wireOp",EDGE,"E16.MirrorCS");var subQ2=makeQuery(id+"F0.imprint","INTERSECT",VERTEX,{"derivedFrom":[subQ1,subQ0]});Q17=makeQuery(id+"F0.imprint","IMPRINT",FACE,{"disambiguationData":[TD([[makeQuery(id+"F0.imprint","IMPRINT",EDGE,{"disambiguationData":[TD([[subQ2,1.0]])],"derivedFrom":subQ1}),1.0]])]});}
            extrude(context, id + "F3", {"entities" : qUnion([Q0, Q1, Q2, Q3, Q4, Q5, Q6, Q7, Q8, Q9, Q10, Q11, Q12, Q13, Q14, Q15, Q16, Q17]), "endBound" : BoundingType.SYMMETRIC, "depth" : 3.17 * mm});
        }
        {
            var Q0;
            {var subQ9=sQuery(id+"F0.wireOp",EDGE,"E83");Q0=makeQuery(id+"F0.imprint","IMPRINT",FACE,{"disambiguationData":[TD([[makeQuery(id+"F0.imprint","IMPRINT",EDGE,{"derivedFrom":subQ9}),1.0]])]});}
            var Q1;
            {var subQ0=sQuery(id+"F0.wireOp",EDGE,"E88");Q1=makeQuery(id+"F0.imprint","IMPRINT",FACE,{"disambiguationData":[TD([[makeQuery(id+"F0.imprint","IMPRINT",EDGE,{"derivedFrom":subQ0}),1.0]])]});}
            var Q2;
            {var subQ2=sQuery(id+"F0.wireOp",EDGE,"E88");Q2=makeQuery(id+"F0.imprint","IMPRINT",FACE,{"disambiguationData":[TD([[makeQuery(id+"F0.imprint","IMPRINT",EDGE,{"derivedFrom":subQ2}),-1.0]])]});}
            var Q3;
            {var subQ0=sQuery(id+"F0.wireOp",EDGE,"E32.MirrorCS");var subQ1=sQuery(id+"F0.wireOp",EDGE,"E29.MirrorCS");var subQ2=makeQuery(id+"F0.imprint","INTERSECT",VERTEX,{"derivedFrom":[subQ1,subQ0]});Q3=makeQuery(id+"F0.imprint","IMPRINT",FACE,{"disambiguationData":[TD([[makeQuery(id+"F0.imprint","IMPRINT",EDGE,{"disambiguationData":[TD([[subQ2,-1.0]])],"derivedFrom":subQ1}),1.0]])]});}
            var Q4;
            {var subQ0=sQuery(id+"F0.wireOp",EDGE,"E32.MirrorCS");var subQ1=sQuery(id+"F0.wireOp",EDGE,"E31.MirrorCS");var subQ2=makeQuery(id+"F0.imprint","INTERSECT",VERTEX,{"derivedFrom":[subQ1,subQ0]});Q4=makeQuery(id+"F0.imprint","IMPRINT",FACE,{"disambiguationData":[TD([[makeQuery(id+"F0.imprint","IMPRINT",EDGE,{"disambiguationData":[TD([[subQ2,-1.0]])],"derivedFrom":subQ1}),-1.0]])]});}
            var Q5;
            {var subQ0=sQuery(id+"F0.wireOp",EDGE,"E31.MirrorCS");var subQ1=sQuery(id+"F0.wireOp",EDGE,"E28.MirrorCS");var subQ2=makeQuery(id+"F0.imprint","INTERSECT",VERTEX,{"derivedFrom":[subQ1,subQ0]});Q5=makeQuery(id+"F0.imprint","IMPRINT",FACE,{"disambiguationData":[TD([[makeQuery(id+"F0.imprint","IMPRINT",EDGE,{"disambiguationData":[TD([[subQ2,-1.0]])],"derivedFrom":subQ1}),-1.0]])]});}
            var Q6;
            {var subQ0=sQuery(id+"F0.wireOp",EDGE,"E29.MirrorCS");var subQ1=sQuery(id+"F0.wireOp",EDGE,"E28.MirrorCS");var subQ2=makeQuery(id+"F0.imprint","INTERSECT",VERTEX,{"derivedFrom":[subQ1,subQ0]});Q6=makeQuery(id+"F0.imprint","IMPRINT",FACE,{"disambiguationData":[TD([[makeQuery(id+"F0.imprint","IMPRINT",EDGE,{"disambiguationData":[TD([[subQ2,1.0]])],"derivedFrom":subQ1}),-1.0]])]});}
            var Q7;
            {var subQ0=sQuery(id+"F0.wireOp",EDGE,"E4.right");var subQ1=sQuery(id+"F0.wireOp",EDGE,"E4.bottom");var subQ2=makeQuery(id+"F0.imprint","INTERSECT",VERTEX,{"derivedFrom":[subQ1,subQ0]});Q7=makeQuery(id+"F0.imprint","IMPRINT",FACE,{"disambiguationData":[TD([[makeQuery(id+"F0.imprint","IMPRINT",EDGE,{"disambiguationData":[TD([[subQ2,1.0]])],"derivedFrom":subQ1}),1.0]])]});}
            var Q8;
            {var subQ0=sQuery(id+"F0.wireOp",EDGE,"E4.left");var subQ1=sQuery(id+"F0.wireOp",EDGE,"E4.bottom");var subQ2=makeQuery(id+"F0.imprint","INTERSECT",VERTEX,{"derivedFrom":[subQ1,subQ0]});Q8=makeQuery(id+"F0.imprint","IMPRINT",FACE,{"disambiguationData":[TD([[makeQuery(id+"F0.imprint","IMPRINT",EDGE,{"disambiguationData":[TD([[subQ2,-1.0]])],"derivedFrom":subQ1}),1.0]])]});}
            var Q9;
            {var subQ0=sQuery(id+"F0.wireOp",EDGE,"E4.left");var subQ1=sQuery(id+"F0.wireOp",EDGE,"E4.top");var subQ2=makeQuery(id+"F0.imprint","INTERSECT",VERTEX,{"derivedFrom":[subQ1,subQ0]});Q9=makeQuery(id+"F0.imprint","IMPRINT",FACE,{"disambiguationData":[TD([[makeQuery(id+"F0.imprint","IMPRINT",EDGE,{"disambiguationData":[TD([[subQ2,-1.0]])],"derivedFrom":subQ1}),-1.0]])]});}
            var Q10;
            {var subQ0=sQuery(id+"F0.wireOp",EDGE,"E4.right");var subQ1=sQuery(id+"F0.wireOp",EDGE,"E4.top");var subQ2=makeQuery(id+"F0.imprint","INTERSECT",VERTEX,{"derivedFrom":[subQ1,subQ0]});Q10=makeQuery(id+"F0.imprint","IMPRINT",FACE,{"disambiguationData":[TD([[makeQuery(id+"F0.imprint","IMPRINT",EDGE,{"disambiguationData":[TD([[subQ2,1.0]])],"derivedFrom":subQ1}),-1.0]])]});}
            var Q11;
            {var subQ13=sQuery(id+"F0.wireOp",EDGE,"E84");Q11=makeQuery(id+"F0.imprint","IMPRINT",FACE,{"disambiguationData":[TD([[makeQuery(id+"F0.imprint","IMPRINT",EDGE,{"derivedFrom":subQ13}),-1.0]])]});}
            var Q12;
            {var subQ0=sQuery(id+"F0.wireOp",EDGE,"E7.MirrorCS");var subQ1=sQuery(id+"F0.wireOp",EDGE,"E6.MirrorCS");var subQ2=makeQuery(id+"F0.imprint","INTERSECT",VERTEX,{"derivedFrom":[subQ1,subQ0]});Q12=makeQuery(id+"F0.imprint","IMPRINT",FACE,{"disambiguationData":[TD([[makeQuery(id+"F0.imprint","IMPRINT",EDGE,{"disambiguationData":[TD([[subQ2,-1.0]])],"derivedFrom":subQ1}),-1.0]])]});}
            var Q13;
            {var subQ0=sQuery(id+"F0.wireOp",EDGE,"E6.MirrorCS");var subQ1=sQuery(id+"F0.wireOp",EDGE,"E5.MirrorCS");var subQ2=makeQuery(id+"F0.imprint","INTERSECT",VERTEX,{"derivedFrom":[subQ1,subQ0]});Q13=makeQuery(id+"F0.imprint","IMPRINT",FACE,{"disambiguationData":[TD([[makeQuery(id+"F0.imprint","IMPRINT",EDGE,{"disambiguationData":[TD([[subQ2,-1.0]])],"derivedFrom":subQ1}),-1.0]])]});}
            var Q14;
            {var subQ0=sQuery(id+"F0.wireOp",EDGE,"E8.MirrorCS");var subQ1=sQuery(id+"F0.wireOp",EDGE,"E5.MirrorCS");var subQ2=makeQuery(id+"F0.imprint","INTERSECT",VERTEX,{"derivedFrom":[subQ1,subQ0]});Q14=makeQuery(id+"F0.imprint","IMPRINT",FACE,{"disambiguationData":[TD([[makeQuery(id+"F0.imprint","IMPRINT",EDGE,{"disambiguationData":[TD([[subQ2,1.0]])],"derivedFrom":subQ1}),-1.0]])]});}
            var Q15;
            {var subQ0=sQuery(id+"F0.wireOp",EDGE,"E8.MirrorCS");var subQ1=sQuery(id+"F0.wireOp",EDGE,"E7.MirrorCS");var subQ2=makeQuery(id+"F0.imprint","INTERSECT",VERTEX,{"derivedFrom":[subQ1,subQ0]});Q15=makeQuery(id+"F0.imprint","IMPRINT",FACE,{"disambiguationData":[TD([[makeQuery(id+"F0.imprint","IMPRINT",EDGE,{"disambiguationData":[TD([[subQ2,1.0]])],"derivedFrom":subQ1}),1.0]])]});}
            var Q16;
            {var subQ0=sQuery(id+"F0.wireOp",EDGE,"E36.MirrorCS");var subQ1=sQuery(id+"F0.wireOp",EDGE,"E33.MirrorCS");var subQ2=makeQuery(id+"F0.imprint","INTERSECT",VERTEX,{"derivedFrom":[subQ1,subQ0]});Q16=makeQuery(id+"F0.imprint","IMPRINT",FACE,{"disambiguationData":[TD([[makeQuery(id+"F0.imprint","IMPRINT",EDGE,{"disambiguationData":[TD([[subQ2,-1.0]])],"derivedFrom":subQ1}),1.0]])]});}
            var Q17;
            {var subQ0=sQuery(id+"F0.wireOp",EDGE,"E36.MirrorCS");var subQ1=sQuery(id+"F0.wireOp",EDGE,"E35.MirrorCS");var subQ2=makeQuery(id+"F0.imprint","INTERSECT",VERTEX,{"derivedFrom":[subQ1,subQ0]});Q17=makeQuery(id+"F0.imprint","IMPRINT",FACE,{"disambiguationData":[TD([[makeQuery(id+"F0.imprint","IMPRINT",EDGE,{"disambiguationData":[TD([[subQ2,-1.0]])],"derivedFrom":subQ1}),-1.0]])]});}
            var Q18;
            {var subQ0=sQuery(id+"F0.wireOp",EDGE,"E37.MirrorCS");var subQ1=sQuery(id+"F0.wireOp",EDGE,"E35.MirrorCS");var subQ2=makeQuery(id+"F0.imprint","INTERSECT",VERTEX,{"derivedFrom":[subQ1,subQ0]});Q18=makeQuery(id+"F0.imprint","IMPRINT",FACE,{"disambiguationData":[TD([[makeQuery(id+"F0.imprint","IMPRINT",EDGE,{"disambiguationData":[TD([[subQ2,1.0]])],"derivedFrom":subQ1}),-1.0]])]});}
            var Q19;
            {var subQ0=sQuery(id+"F0.wireOp",EDGE,"E37.MirrorCS");var subQ1=sQuery(id+"F0.wireOp",EDGE,"E33.MirrorCS");var subQ2=makeQuery(id+"F0.imprint","INTERSECT",VERTEX,{"derivedFrom":[subQ1,subQ0]});Q19=makeQuery(id+"F0.imprint","IMPRINT",FACE,{"disambiguationData":[TD([[makeQuery(id+"F0.imprint","IMPRINT",EDGE,{"disambiguationData":[TD([[subQ2,1.0]])],"derivedFrom":subQ1}),1.0]])]});}
            extrude(context, id + "F4", {"entities" : qUnion([Q0, Q1, Q2, Q3, Q4, Q5, Q6, Q7, Q8, Q9, Q10, Q11, Q12, Q13, Q14, Q15, Q16, Q17, Q18, Q19]), "endBound" : BoundingType.SYMMETRIC, "depth" : 3.17 * mm});
        }
    });
